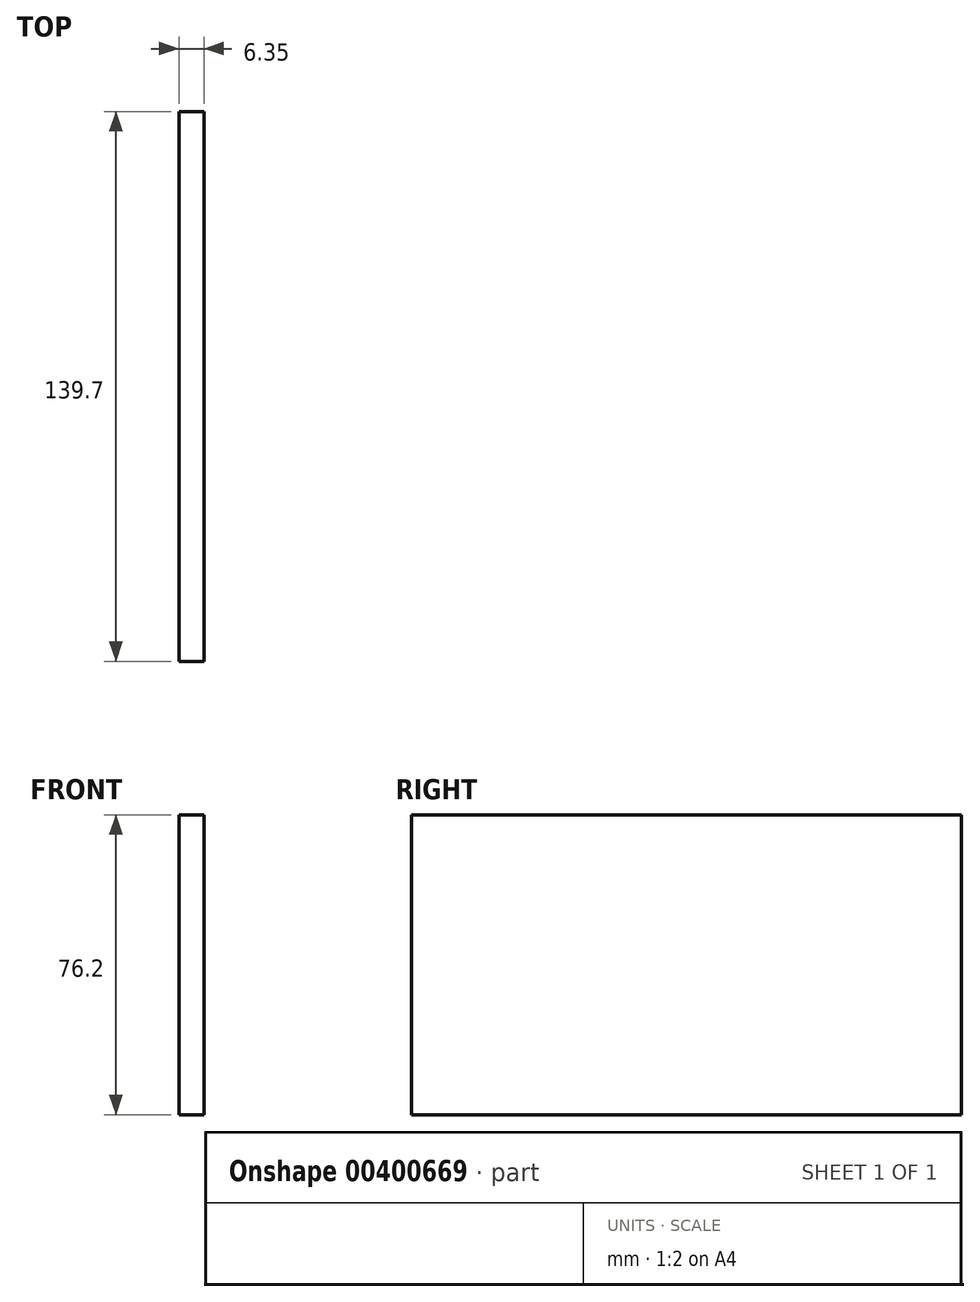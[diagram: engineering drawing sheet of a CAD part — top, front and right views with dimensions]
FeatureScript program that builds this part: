
annotation { "Feature Type Name" : "Feature", "Feature Type Description" : "" }
export const myFeature = defineFeature(function(context is Context, id is Id, definition is map)
    precondition{}
    {
        {
            var Q0;
            Q0=qCreatedBy(makeId("Right.planeOp"),FACE);
            var sketch = newSketch(context, id + "F0", { "sketchPlane" : qUnion([Q0])});
            skLineSegment(sketch, "E0", {"start": v(0, 0) * mm, "end": v(139.7, 0) * mm});
            skLineSegment(sketch, "E1", {"start": v(0, 0) * mm, "end": v(0, 76.2) * mm});
            skLineSegment(sketch, "E2", {"start": v(139.7, 0) * mm, "end": v(139.7, 76.2) * mm});
            skLineSegment(sketch, "E3", {"start": v(139.7, 76.2) * mm, "end": v(0, 76.2) * mm});
            skSolve(sketch);
        }
        {
            var Q0;
            Q0 = qSketchRegion(id + "F0", true);
            extrude(context, id + "F1", {"entities" : qUnion([Q0]), "depth" : 6.35 * mm});
        }
    });
